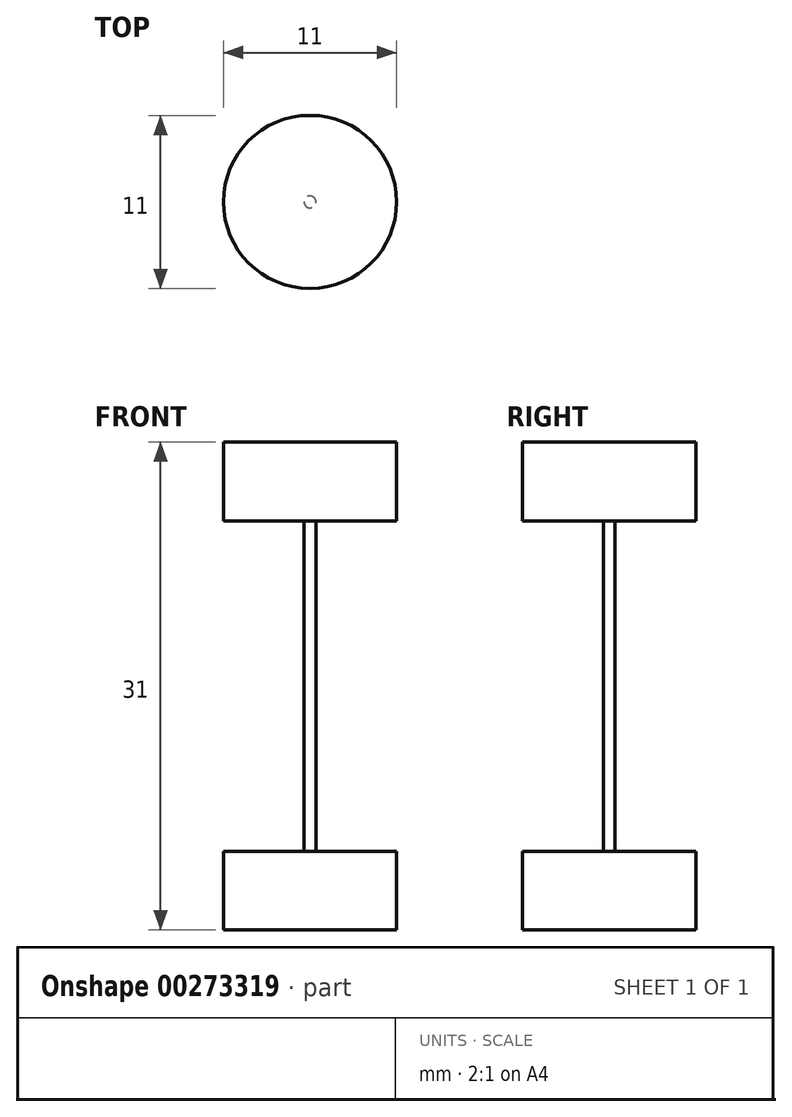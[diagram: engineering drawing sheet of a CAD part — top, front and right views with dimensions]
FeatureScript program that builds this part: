
annotation { "Feature Type Name" : "Feature", "Feature Type Description" : "" }
export const myFeature = defineFeature(function(context is Context, id is Id, definition is map)
    precondition{}
    {
        {
            var Q0;
            Q0=qCreatedBy(makeId("Top.planeOp"),FACE);
            var sketch = newSketch(context, id + "F0", { "sketchPlane" : qUnion([Q0])});
            skCircle(sketch, "E0", {"center": v(0, 0) * mm, "radius": 5.5 * mm});
            skSolve(sketch);
        }
        {
            var Q0;
            Q0=makeQuery(id+"F0.imprint","IMPRINT",FACE,{"disambiguationData":[TD([[makeQuery(id+"F0.imprint","IMPRINT",EDGE,{"derivedFrom":sQuery(id+"F0.wireOp",EDGE,"E0")}),1.0]])]});
            extrude(context, id + "F1", {"entities" : qUnion([Q0]), "depth" : 5 * mm});
        }
        {
            var Q0;
            Q0=makeQuery(id+"F1.opExtrude","CAP_FACE",FACE,{"disambiguationData":[OSD([sQuery(id+"F0.wireOp",EDGE,"E0")])],"isStart":true});
            cPlane(context, id + "F2", {"entities" : qUnion([Q0]), "cplaneType" : CPlaneType.OFFSET, "offset" : 21 * mm, "width" : 150 * mm, "height" : 150 * mm});
        }
        {
            var Q0;
            Q0=qCreatedBy(id+"F2.planeOp",FACE);
            var sketch = newSketch(context, id + "F3", { "sketchPlane" : qUnion([Q0])});
            skCircle(sketch, "E1.0.0", {"center": v(0, 0) * mm, "radius": 5.5 * mm});
            skSolve(sketch);
        }
        {
            var Q0;
            Q0=makeQuery(id+"F3.imprint","IMPRINT",FACE,{"disambiguationData":[TD([[makeQuery(id+"F3.imprint","IMPRINT",EDGE,{"derivedFrom":sQuery(id+"F3.wireOp",EDGE,"E1.0.0")}),1.0]])]});
            extrude(context, id + "F4", {"entities" : qUnion([Q0]), "depth" : 5 * mm});
        }
        {
            var Q0;
            Q0=makeQuery(id+"F1.opExtrude","CAP_FACE",FACE,{"disambiguationData":[OSD([sQuery(id+"F0.wireOp",EDGE,"E0")])],"isStart":true});
            var sketch = newSketch(context, id + "F5", { "sketchPlane" : qUnion([Q0])});
            skPoint(sketch, "E2.0", {"position": v(0, 0) * mm});
            skCircle(sketch, "E3", {"center": v(0, 0) * mm, "radius": 0.38 * mm});
            skSolve(sketch);
        }
        {
            var Q0;
            Q0=makeQuery(id+"F5.imprint","IMPRINT",FACE,{"disambiguationData":[TD([[makeQuery(id+"F5.imprint","IMPRINT",EDGE,{"derivedFrom":sQuery(id+"F5.wireOp",EDGE,"E3")}),1.0]])]});
            extrude(context, id + "F6", {"entities" : qUnion([Q0]), "depth" : 21 * mm});
        }
    });
